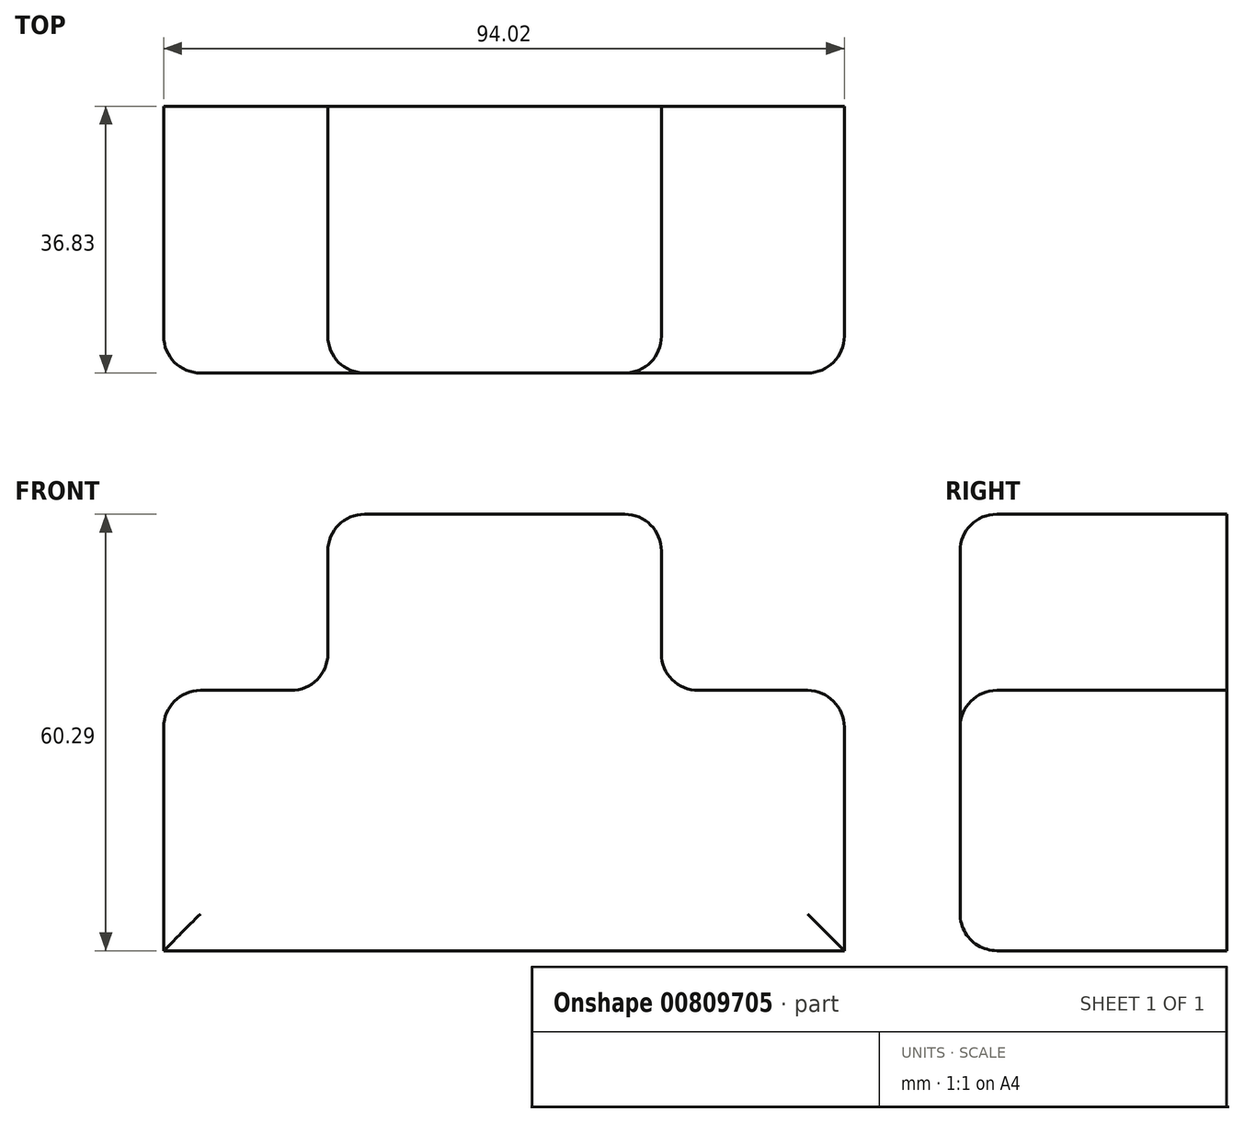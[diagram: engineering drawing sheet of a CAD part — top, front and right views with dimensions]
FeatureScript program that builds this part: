
annotation { "Feature Type Name" : "Feature", "Feature Type Description" : "" }
export const myFeature = defineFeature(function(context is Context, id is Id, definition is map)
    precondition{}
    {
        {
            var Q0;
            Q0=qCreatedBy(makeId("Front.planeOp"),FACE);
            var sketch = newSketch(context, id + "F0", { "sketchPlane" : qUnion([Q0])});
            skLineSegment(sketch, "E0.bottom", {"start": v(-42.86, 15.76) * mm, "end": v(-20.19, 15.76) * mm});
            skLineSegment(sketch, "E0.top", {"start": v(-42.86, -20.19) * mm, "end": v(51.16, -20.19) * mm});
            skLineSegment(sketch, "E0.left", {"start": v(-42.86, 15.76) * mm, "end": v(-42.86, -20.19) * mm});
            skLineSegment(sketch, "E0.right", {"start": v(51.16, 15.76) * mm, "end": v(51.16, -20.19) * mm});
            skLineSegment(sketch, "E1.bottom", {"start": v(-20.19, 40.1) * mm, "end": v(25.9, 40.1) * mm});
            skLineSegment(sketch, "E1.right", {"start": v(25.9, 40.1) * mm, "end": v(25.9, 15.76) * mm});
            skLineSegment(sketch, "E2", {"start": v(-20.19, 15.76) * mm, "end": v(-20.19, 40.1) * mm});
            skLineSegment(sketch, "E3.trimOffspring", {"start": v(25.9, 15.76) * mm, "end": v(51.16, 15.76) * mm});
            skSolve(sketch);
        }
        {
            var Q0;
            Q0=makeQuery(id+"F0.imprint","IMPRINT",FACE,{"disambiguationData":[TD([[makeQuery(id+"F0.imprint","IMPRINT",EDGE,{"derivedFrom":sQuery(id+"F0.wireOp",EDGE,"E0.bottom")}),-1.0]])]});
            extrude(context, id + "F1", {"entities" : qUnion([Q0]), "depth" : 36.83 * mm, "offsetDistance" : 25.4 * mm});
        }
        {
            var Q0;
            Q0=makeQuery(id+"F1.opExtrude","SWEPT_EDGE",EDGE,{"disambiguationData":[OSD([sQuery(id+"F0.wireOp",EDGE,"E1.bottom"),sQuery(id+"F0.wireOp",EDGE,"E1.right")])]});
            var Q1;
            Q1=makeQuery(id+"F1.opExtrude","SWEPT_EDGE",EDGE,{"disambiguationData":[OSD([sQuery(id+"F0.wireOp",EDGE,"E1.bottom"),sQuery(id+"F0.wireOp",EDGE,"E2")])]});
            var Q2;
            Q2=makeQuery(id+"F1.opExtrude","SWEPT_EDGE",EDGE,{"disambiguationData":[OSD([sQuery(id+"F0.wireOp",EDGE,"E0.right"),sQuery(id+"F0.wireOp",EDGE,"E3.trimOffspring")])]});
            var Q3;
            Q3=makeQuery(id+"F1.opExtrude","SWEPT_EDGE",EDGE,{"disambiguationData":[OSD([sQuery(id+"F0.wireOp",EDGE,"E1.right"),sQuery(id+"F0.wireOp",EDGE,"E3.trimOffspring")])]});
            var Q4;
            Q4=makeQuery(id+"F1.opExtrude","SWEPT_EDGE",EDGE,{"disambiguationData":[OSD([sQuery(id+"F0.wireOp",EDGE,"E0.bottom"),sQuery(id+"F0.wireOp",EDGE,"E2")])]});
            var Q5;
            Q5=makeQuery(id+"F1.opExtrude","SWEPT_EDGE",EDGE,{"disambiguationData":[OSD([sQuery(id+"F0.wireOp",EDGE,"E0.bottom"),sQuery(id+"F0.wireOp",EDGE,"E0.left")])]});
            fillet(context, id + "F2", {"entities" : qUnion([Q0, Q1, Q2, Q3, Q4, Q5]), "radius" : 5.08 * mm, "tangentPropagation" : true, "allowEdgeOverflow" : false});
        }
        {
            var Q0;
            Q0=makeQuery(id+"F1.opExtrude","CAP_FACE",FACE,{"disambiguationData":[OSD([sQuery(id+"F0.wireOp",EDGE,"E0.bottom"),sQuery(id+"F0.wireOp",EDGE,"E0.top"),sQuery(id+"F0.wireOp",EDGE,"E0.left"),sQuery(id+"F0.wireOp",EDGE,"E0.right"),sQuery(id+"F0.wireOp",EDGE,"E1.bottom"),sQuery(id+"F0.wireOp",EDGE,"E1.right"),sQuery(id+"F0.wireOp",EDGE,"E2"),sQuery(id+"F0.wireOp",EDGE,"E3.trimOffspring")])],"isStart":false});
            fillet(context, id + "F3", {"entities" : qUnion([Q0]), "radius" : 5.08 * mm, "tangentPropagation" : true, "allowEdgeOverflow" : false});
        }
    });
